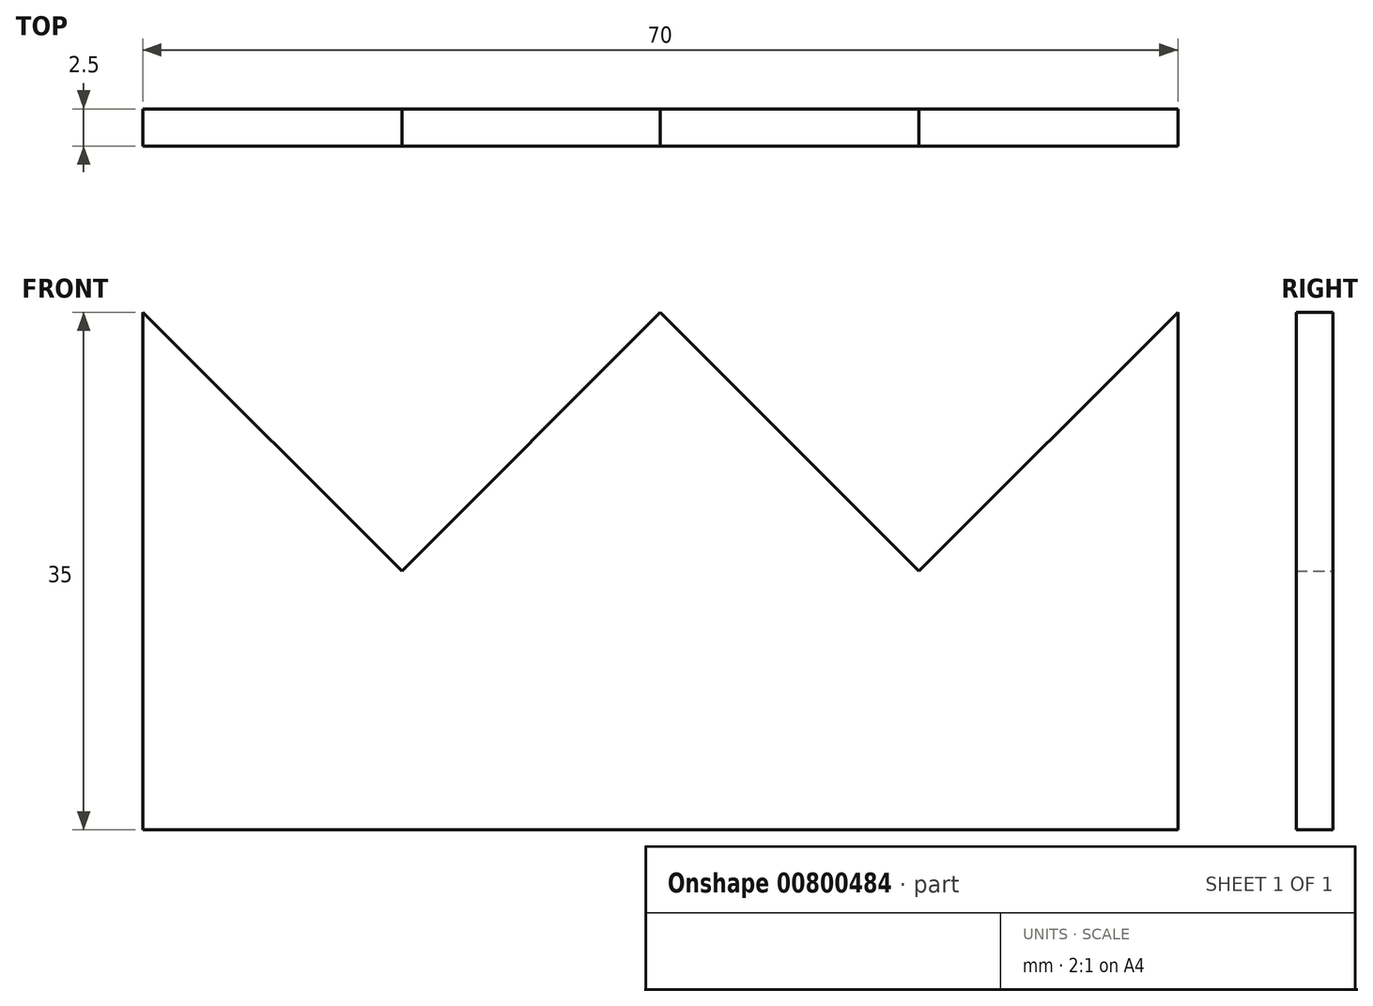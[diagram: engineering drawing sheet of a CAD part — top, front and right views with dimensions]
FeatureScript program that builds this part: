
annotation { "Feature Type Name" : "Feature", "Feature Type Description" : "" }
export const myFeature = defineFeature(function(context is Context, id is Id, definition is map)
    precondition{}
    {
        {
            var Q0;
            Q0=qCreatedBy(makeId("Front.planeOp"),FACE);
            var sketch = newSketch(context, id + "F0", { "sketchPlane" : qUnion([Q0])});
            skLineSegment(sketch, "E0.top", {"start": v(-35, -17.5) * mm, "end": v(35, -17.5) * mm});
            skLineSegment(sketch, "E0.left", {"start": v(-35, 17.5) * mm, "end": v(-35, -17.5) * mm});
            skLineSegment(sketch, "E0.right", {"start": v(35, 17.5) * mm, "end": v(35, -17.5) * mm});
            skPoint(sketch, "E0.middle", {"position": v(0, 0) * mm});
            skLineSegment(sketch, "E1", {"start": v(-35, 17.5) * mm, "end": v(-17.49, 0) * mm});
            skLineSegment(sketch, "E2", {"start": v(-17.49, 0) * mm, "end": v(0, 17.5) * mm});
            skLineSegment(sketch, "E3.MirrorCS", {"start": v(35, 17.5) * mm, "end": v(17.49, 0) * mm});
            skLineSegment(sketch, "E4.MirrorCS", {"start": v(17.49, 0) * mm, "end": v(0, 17.5) * mm});
            skSolve(sketch);
        }
        {
            var Q0;
            Q0=makeQuery(id+"F0.imprint","IMPRINT",FACE,{"disambiguationData":[TD([[makeQuery(id+"F0.imprint","IMPRINT",EDGE,{"derivedFrom":sQuery(id+"F0.wireOp",EDGE,"E0.top")}),1.0]])]});
            extrude(context, id + "F1", {"entities" : qUnion([Q0]), "depth" : 2.5 * mm, "offsetDistance" : 25 * mm});
        }
    });
